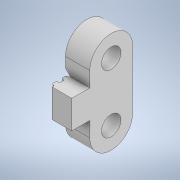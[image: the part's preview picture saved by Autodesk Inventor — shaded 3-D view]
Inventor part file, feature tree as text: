
AUTODESK INVENTOR PART (.ipt)
format: ipt  version: 2022 (Build 260153000, 153)  size: 220,672 bytes
history: native  units: mm
features: extrude x3, sketch x3, chamfer x1, fillet x1, projected_geometry x1
ambient origin geometry x8: Origin, YZ Plane, XZ Plane, XY Plane, X Axis, Y Axis, Z Axis, Center Point
bodies: Solid1 (feature_tree)
feature tree (9):
  extrude  "Extrusion1"  Depth=4.0mm
  extrude  "Extrusion2"  Depth=8.8mm
  chamfer  "Chamfer1"  Distance=5.8mm
  extrude  "Extrusion3"  Depth=0.3mm
  fillet  "Fillet1"  Radius=5.0mm
  sketch  "Sketch1"  dims[d0=4.0mm d1=4.0mm]
  sketch  "Sketch2"  dims[d2=12.0mm d3=8.8mm]
  sketch  "Sketch3"  dims[d4=8.8mm d5=5.8mm d6=3.1mm d7=5.0mm d8=0.0mm d9=0.0mm d10=1.0mm d11=0.0mm d12=1.0mm d13=2.0mm d14=45.0deg d15=1.0mm d16=1.0mm d17=60.0mm d19=2.0mm d20=10.0mm d22=10.0mm d24=0.6mm d25=0.0mm d26=0.3mm]
  projected_geometry  "Projected Loop1"
